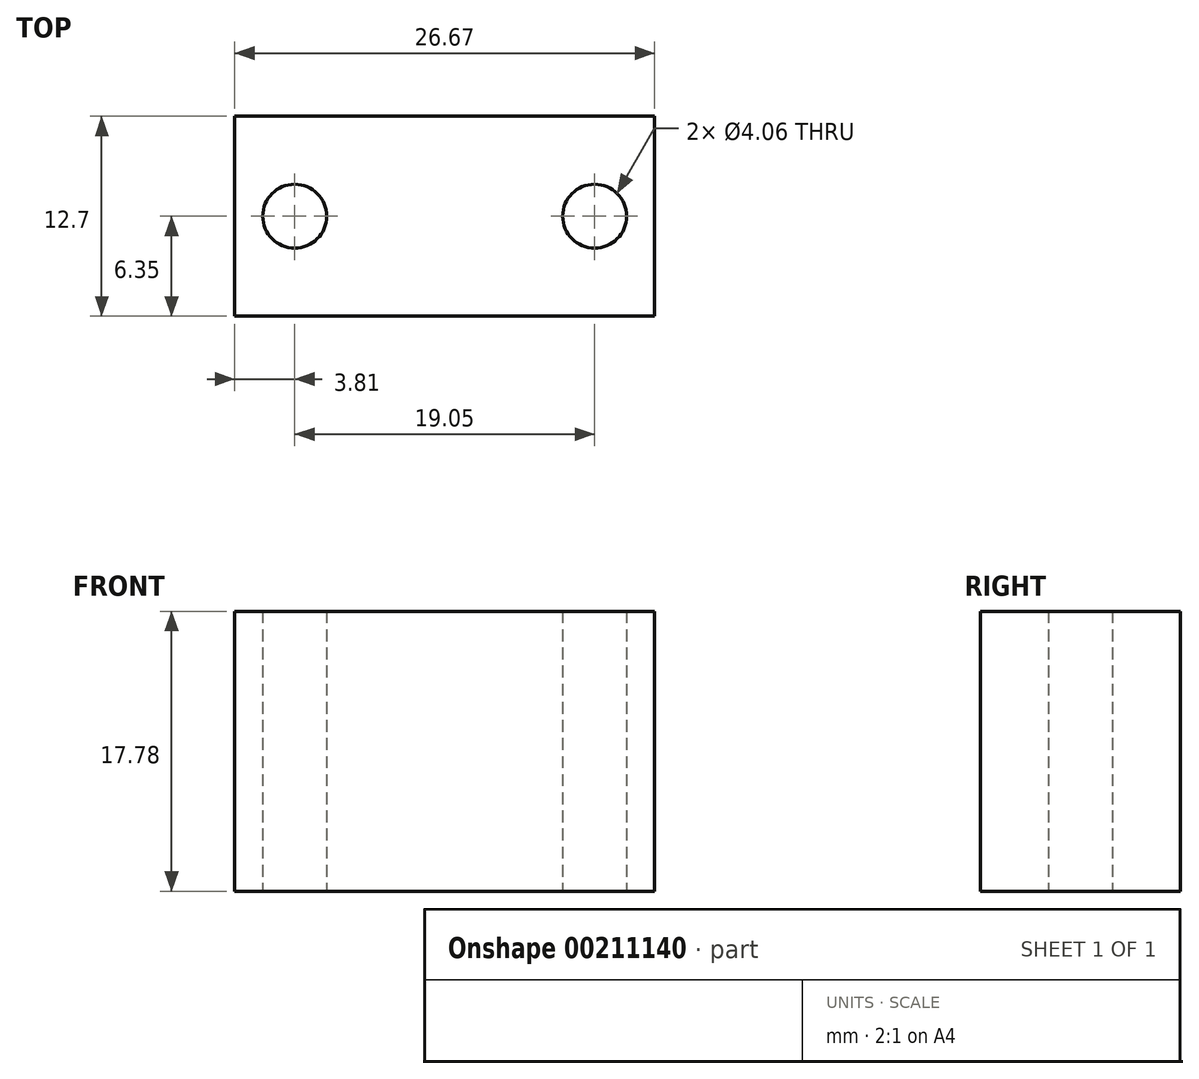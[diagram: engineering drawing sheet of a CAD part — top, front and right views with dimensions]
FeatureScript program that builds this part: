
annotation { "Feature Type Name" : "Feature", "Feature Type Description" : "" }
export const myFeature = defineFeature(function(context is Context, id is Id, definition is map)
    precondition{}
    {
        {
            var Q0;
            Q0=qCreatedBy(makeId("Top.planeOp"),FACE);
            var sketch = newSketch(context, id + "F0", { "sketchPlane" : qUnion([Q0])});
            skLineSegment(sketch, "E0.bottom", {"start": v(0, 0) * mm, "end": v(26.67, 0) * mm});
            skLineSegment(sketch, "E0.top", {"start": v(0, 12.7) * mm, "end": v(26.67, 12.7) * mm});
            skLineSegment(sketch, "E0.left", {"start": v(0, 0) * mm, "end": v(0, 12.7) * mm});
            skLineSegment(sketch, "E0.right", {"start": v(26.67, 0) * mm, "end": v(26.67, 12.7) * mm});
            skCircle(sketch, "E1", {"center": v(22.86, 6.35) * mm, "radius": 2.03 * mm});
            skPoint(sketch, "E1.centerSnap0", {"position": v(26.67, 6.35) * mm});
            skLineSegment(sketch, "E2", {"start": v(13.33, 12.7) * mm, "end": v(13.33, 0) * mm, "construction": true});
            skCircle(sketch, "E3.MirrorC", {"center": v(3.81, 6.35) * mm, "radius": 2.03 * mm});
            skSolve(sketch);
        }
        {
            var Q0;
            Q0 = qSketchRegion(id + "F0", true);
            extrude(context, id + "F1", {"entities" : qUnion([Q0]), "depth" : 17.78 * mm});
        }
    });
